# Revit family: Shower-Bath-American_Standard-Moments-T506.50x_Series
name_source: partatom
category: Plumbing Fixtures
revit_build: Autodesk Revit 2014 (Build: 20130308_1515(x64)
units: mm (PartAtom-declared; Revit-internal decimal feet)

## types (3) — shared parameters
ADA Compliant = Yes
Assembly Code = D2020300
CW Connection = Yes
CWFU = 2
Cold Water Connection Diameter = 1/2"
Cold Water Connection Height = 39"
Cold Water Connection Radius = 1/4"
Default Elevation = 0"
HW Connection = Yes
HWFU = 3
Height = 74"
Hot Water Connection Diameter = 1/2"
Hot Water Connection Height = 39"
Hot Water Connection Radius = 1/4"
Length = 8 1/2"
Manufacturer = American Standard
Material = Brass-American Standard-002-Polished Chrome
NPT Connection Radius = 1/4"
NPT Connection Size = 1/2"
Price = Prices may vary. Please consult Manufacturer Representative for most up-to-date price list.
Product Documentation Link = https://www.americanstandard-us.com
Product Page URL = https://www.americanstandard-us.com
Revised Date = 11/18/2016
URL = http://www.americanstandard-us.com
Valve = Yes
Vent Connection = No
WFU = 4
Warranty Information = Limited Lifetime Function and Finish Warranty.
Waste Connection = No
Width = 6"

## per-type parameters (varying)
| type | Bath | Description | Shower |
| T506.502 | Yes | Moments Pressure Balance Bath-Shower Fitting. Bath and Shower Trim Kit. | Yes |
| T506.501 | No | Moments Pressure Balance Bath-Shower Fitting. Shower Only Trim Kit. | Yes |
| T506.500 | No | Moments Pressure Balance Bath-Shower Fitting. Valve Only Trim Kit. | No |

note: column(s) folded — value = type name in every type: Model

## geometry (parser evidence)
native form markers: Sweep x3
no freeform markers — native parametric forms only
